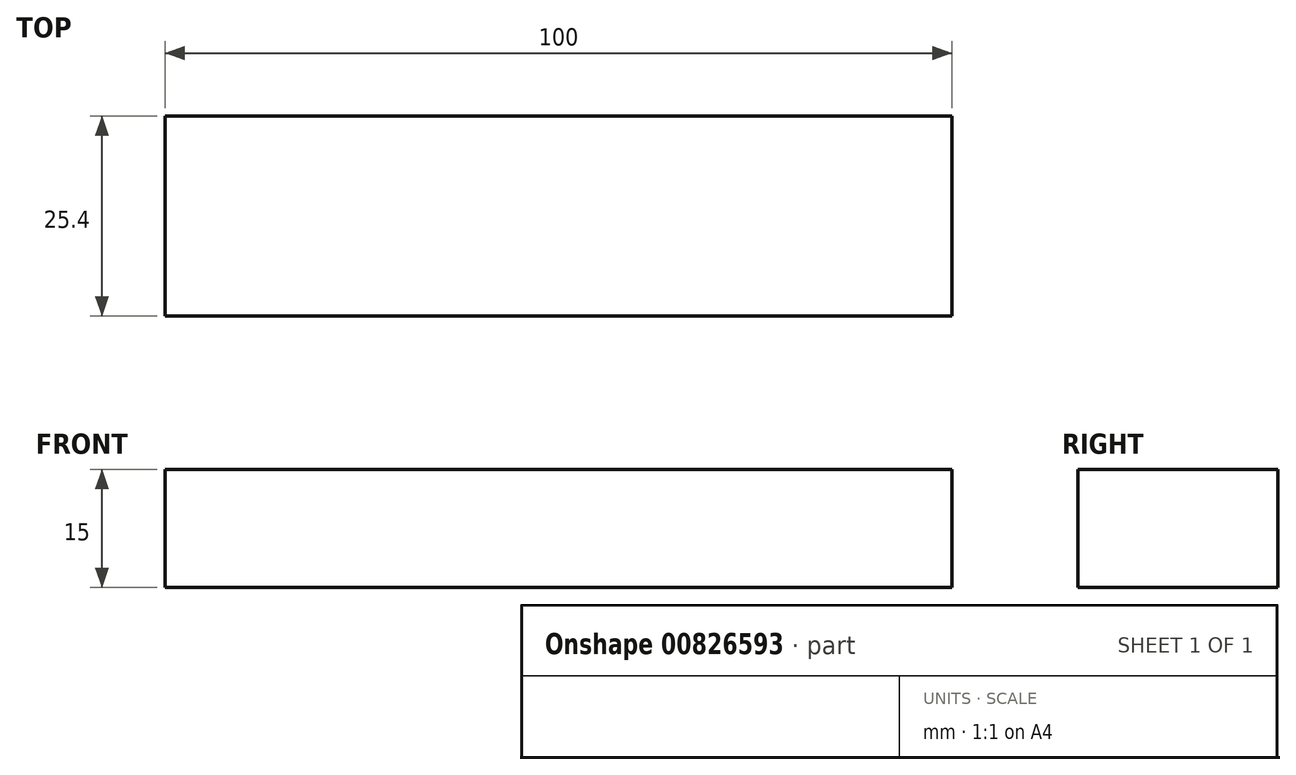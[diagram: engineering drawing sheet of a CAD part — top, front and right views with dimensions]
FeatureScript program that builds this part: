
annotation { "Feature Type Name" : "Feature", "Feature Type Description" : "" }
export const myFeature = defineFeature(function(context is Context, id is Id, definition is map)
    precondition{}
    {
        {
            var Q0;
            Q0=qCreatedBy(makeId("Front.planeOp"),FACE);
            var sketch = newSketch(context, id + "F0", { "sketchPlane" : qUnion([Q0])});
            skLineSegment(sketch, "E0.bottom", {"start": v(-17.54, 0) * mm, "end": v(82.46, 0) * mm});
            skLineSegment(sketch, "E0.top", {"start": v(-17.54, 15) * mm, "end": v(82.46, 15) * mm});
            skLineSegment(sketch, "E0.left", {"start": v(-17.54, 0) * mm, "end": v(-17.54, 15) * mm});
            skLineSegment(sketch, "E0.right", {"start": v(82.46, 0) * mm, "end": v(82.46, 15) * mm});
            skSolve(sketch);
        }
        {
            var Q0;
            Q0=makeQuery(id+"F0.imprint","IMPRINT",FACE,{"disambiguationData":[TD([[makeQuery(id+"F0.imprint","IMPRINT",EDGE,{"derivedFrom":sQuery(id+"F0.wireOp",EDGE,"E0.bottom")}),1.0]])]});
            extrude(context, id + "F1", {"entities" : qUnion([Q0]), "endBound" : BoundingType.SYMMETRIC, "depth" : 25.4 * mm, "offsetDistance" : 25.4 * mm});
        }
    });
